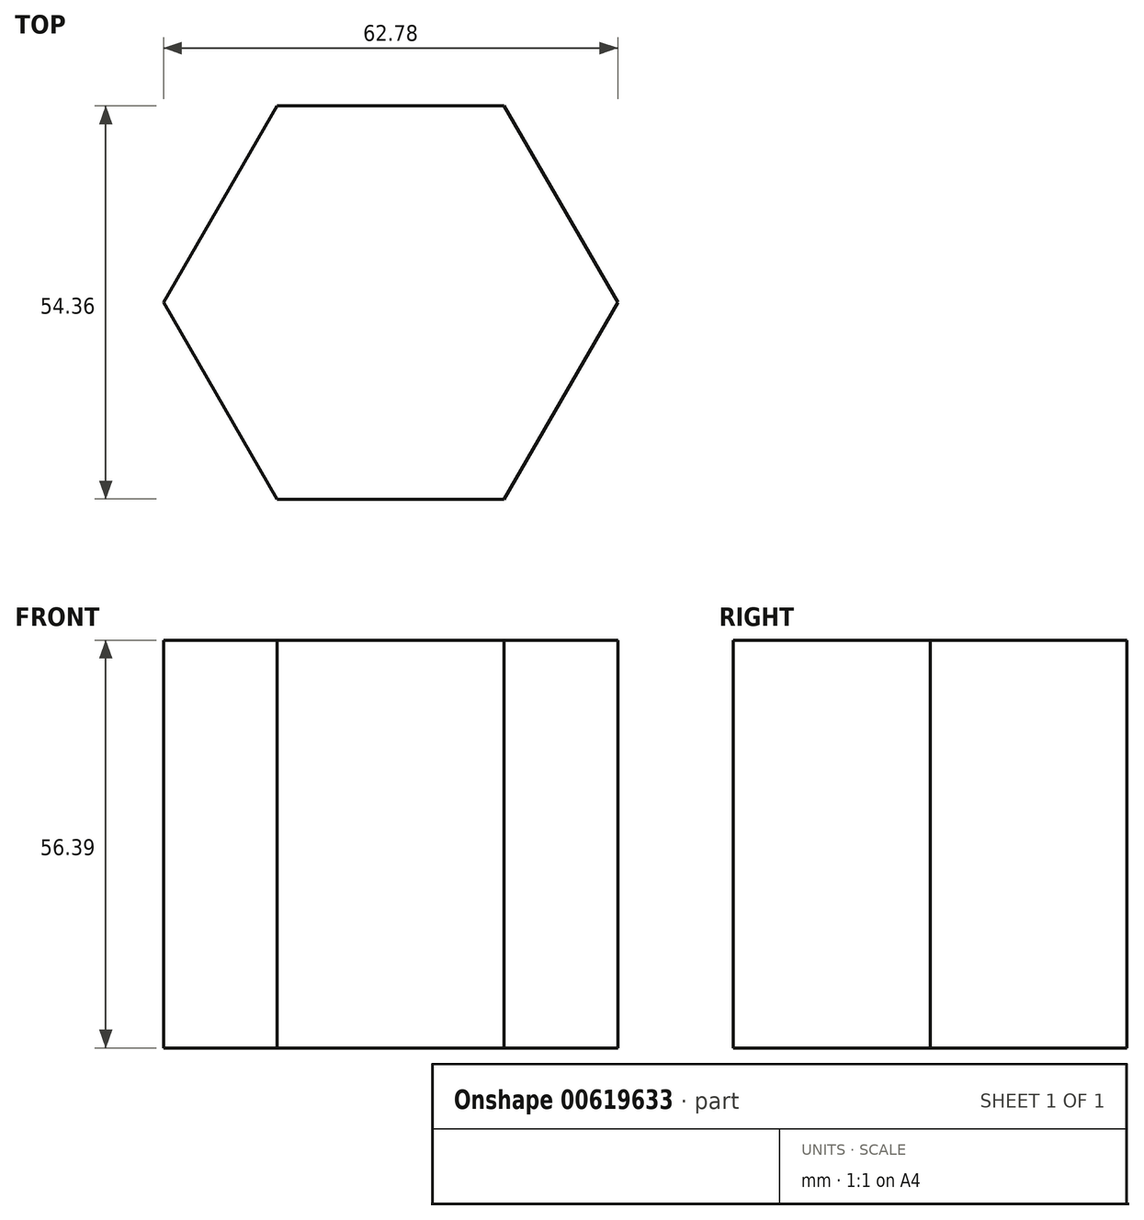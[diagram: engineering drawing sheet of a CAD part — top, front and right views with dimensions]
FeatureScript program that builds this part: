
annotation { "Feature Type Name" : "Feature", "Feature Type Description" : "" }
export const myFeature = defineFeature(function(context is Context, id is Id, definition is map)
    precondition{}
    {
        {
            var Q0;
            Q0=qCreatedBy(makeId("Top.planeOp"),FACE);
            var sketch = newSketch(context, id + "F0", { "sketchPlane" : qUnion([Q0])});
            skCircle(sketch, "E0.cCircle", {"center": v(0, 0) * mm, "radius": 31.39 * mm, "construction": true});
            skLineSegment(sketch, "E0.0", {"start": v(-31.39, 0) * mm, "end": v(-15.7, 27.18) * mm});
            skLineSegment(sketch, "E0.1", {"start": v(-15.7, 27.18) * mm, "end": v(15.7, 27.18) * mm});
            skLineSegment(sketch, "E0.2", {"start": v(15.7, 27.18) * mm, "end": v(31.39, 0) * mm});
            skLineSegment(sketch, "E0.3", {"start": v(31.39, 0) * mm, "end": v(15.7, -27.18) * mm});
            skLineSegment(sketch, "E0.4", {"start": v(15.7, -27.18) * mm, "end": v(-15.7, -27.18) * mm});
            skLineSegment(sketch, "E0.5", {"start": v(-15.7, -27.18) * mm, "end": v(-31.39, 0) * mm});
            skSolve(sketch);
        }
        {
            var Q0;
            Q0=makeQuery(id+"F0.imprint","IMPRINT",FACE,{"disambiguationData":[TD([[makeQuery(id+"F0.imprint","IMPRINT",EDGE,{"derivedFrom":sQuery(id+"F0.wireOp",EDGE,"E0.0")}),-1.0]])]});
            extrude(context, id + "F1", {"entities" : qUnion([Q0]), "depth" : 56.4 * mm, "offsetDistance" : 25.4 * mm});
        }
    });
